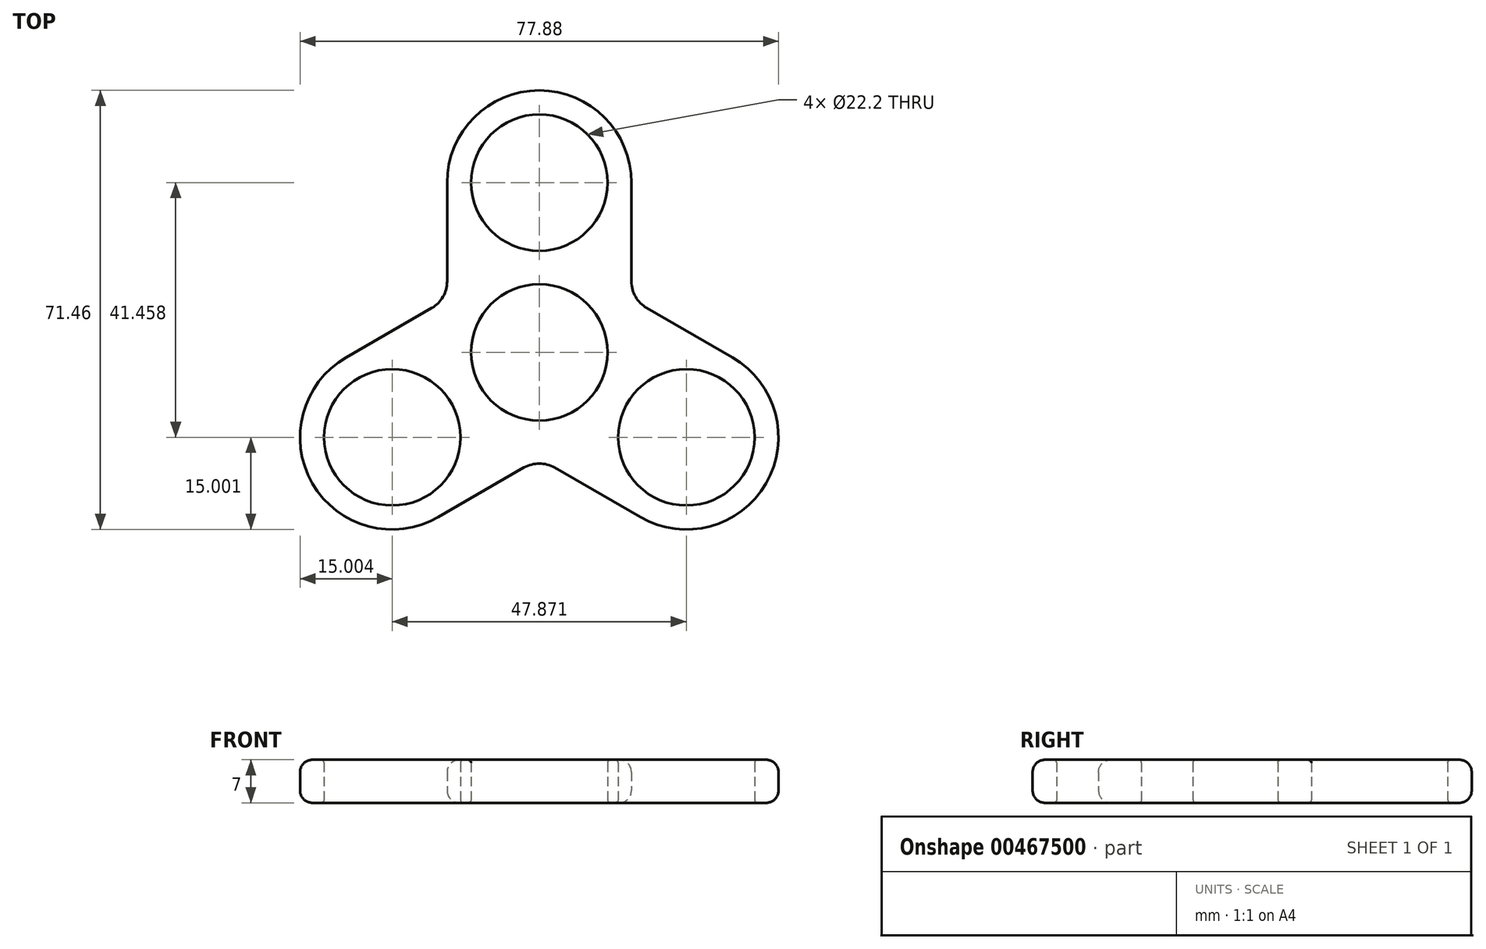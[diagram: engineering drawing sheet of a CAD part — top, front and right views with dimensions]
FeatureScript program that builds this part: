
annotation { "Feature Type Name" : "Feature", "Feature Type Description" : "" }
export const myFeature = defineFeature(function(context is Context, id is Id, definition is map)
    precondition{}
    {
        {
            var Q0;
            Q0=qCreatedBy(makeId("Top.planeOp"),FACE);
            var sketch = newSketch(context, id + "F0", { "sketchPlane" : qUnion([Q0])});
            skCircle(sketch, "E0", {"center": v(0, 27.64) * mm, "radius": 11.1 * mm});
            skLineSegment(sketch, "E1", {"start": v(0, 0) * mm, "end": v(0, 27.64) * mm, "construction": true});
            skCircle(sketch, "E2", {"center": v(0, 27.64) * mm, "radius": 15 * mm});
            skCircle(sketch, "E3", {"center": v(0, 0) * mm, "radius": 11.1 * mm});
            skLineSegment(sketch, "E4", {"start": v(-15, 27.64) * mm, "end": v(-15, 0) * mm});
            skLineSegment(sketch, "E5", {"start": v(15, 27.64) * mm, "end": v(15, 0) * mm});
            skLineSegment(sketch, "E6", {"start": v(-15, 0) * mm, "end": v(15, 0) * mm});
            skCircle(sketch, "E7.1.0", {"center": v(-23.94, -13.82) * mm, "radius": 11.1 * mm});
            skCircle(sketch, "E7.1.1", {"center": v(-23.94, -13.82) * mm, "radius": 15 * mm});
            skLineSegment(sketch, "E7.1.2", {"start": v(-31.44, -0.83) * mm, "end": v(-7.5, 13) * mm});
            skLineSegment(sketch, "E7.1.3", {"start": v(-16.44, -26.8) * mm, "end": v(7.5, -13) * mm});
            skCircle(sketch, "E7.2.0", {"center": v(23.94, -13.82) * mm, "radius": 11.1 * mm});
            skCircle(sketch, "E7.2.1", {"center": v(23.94, -13.82) * mm, "radius": 15 * mm});
            skLineSegment(sketch, "E7.2.2", {"start": v(16.44, -26.8) * mm, "end": v(-7.5, -13) * mm});
            skLineSegment(sketch, "E7.2.3", {"start": v(31.44, -0.83) * mm, "end": v(7.5, 13) * mm});
            skSolve(sketch);
        }
        {
            var Q0;
            Q0=makeQuery(id+"F0.imprint","IMPRINT",FACE,{"disambiguationData":[TD([[makeQuery(id+"F0.imprint","IMPRINT",EDGE,{"derivedFrom":sQuery(id+"F0.wireOp",EDGE,"E7.1.0")}),-1.0]])]});
            var Q1;
            {var subQ7=sQuery(id+"F0.wireOp",EDGE,"E6");var subQ10=sQuery(id+"F0.wireOp",EDGE,"E3");var subQ14=makeQuery(id+"F0.imprint","INTERSECT",VERTEX,{"disambiguationData":[OD(0.0)],"derivedFrom":[subQ10,subQ7]});Q1=makeQuery(id+"F0.imprint","IMPRINT",FACE,{"disambiguationData":[TD([[makeQuery(id+"F0.imprint","IMPRINT",EDGE,{"disambiguationData":[TD([[subQ14,-1.0]])],"derivedFrom":subQ10}),-1.0]])]});}
            var Q2;
            Q2=makeQuery(id+"F0.imprint","IMPRINT",FACE,{"disambiguationData":[TD([[makeQuery(id+"F0.imprint","IMPRINT",EDGE,{"derivedFrom":sQuery(id+"F0.wireOp",EDGE,"E7.2.0")}),-1.0]])]});
            var Q3;
            {var subQ1=sQuery(id+"F0.wireOp",EDGE,"E4");var subQ4=sQuery(id+"F0.wireOp",EDGE,"E2");var subQ5=makeQuery(id+"F0.imprint","INTERSECT",VERTEX,{"derivedFrom":[subQ4,subQ1]});Q3=makeQuery(id+"F0.imprint","IMPRINT",FACE,{"disambiguationData":[TD([[makeQuery(id+"F0.imprint","IMPRINT",EDGE,{"disambiguationData":[TD([[subQ5,-1.0]])],"derivedFrom":subQ4}),-1.0]])]});}
            var Q4;
            Q4=makeQuery(id+"F0.imprint","IMPRINT",FACE,{"disambiguationData":[TD([[makeQuery(id+"F0.imprint","IMPRINT",EDGE,{"derivedFrom":sQuery(id+"F0.wireOp",EDGE,"E0")}),-1.0]])]});
            extrude(context, id + "F1", {"entities" : qUnion([Q0, Q1, Q2, Q3, Q4]), "depth" : 7 * mm});
        }
        {
            var Q0;
            Q0=makeQuery(id+"F1.opExtrude","SWEPT_EDGE",EDGE,{"disambiguationData":[OSD([sQuery(id+"F0.wireOp",EDGE,"E4"),sQuery(id+"F0.wireOp",EDGE,"E7.1.2")])]});
            var Q1;
            Q1=makeQuery(id+"F1.opExtrude","SWEPT_EDGE",EDGE,{"disambiguationData":[OSD([sQuery(id+"F0.wireOp",EDGE,"E5"),sQuery(id+"F0.wireOp",EDGE,"E7.2.3")])]});
            var Q2;
            Q2=makeQuery(id+"F1.opExtrude","SWEPT_EDGE",EDGE,{"disambiguationData":[OSD([sQuery(id+"F0.wireOp",EDGE,"E7.1.3"),sQuery(id+"F0.wireOp",EDGE,"E7.2.2")])]});
            fillet(context, id + "F2", {"entities" : qUnion([Q0, Q1, Q2]), "radius" : 5 * mm, "tangentPropagation" : true, "allowEdgeOverflow" : false});
        }
        {
            var Q0;
            Q0=makeQuery(id+"F1.opExtrude","CAP_EDGE",EDGE,{"disambiguationData":[OSD([sQuery(id+"F0.wireOp",EDGE,"E0")])],"isStart":false});
            var Q1;
            Q1=makeQuery(id+"F1.opExtrude","CAP_EDGE",EDGE,{"disambiguationData":[OSD([sQuery(id+"F0.wireOp",EDGE,"E3")])],"isStart":false});
            var Q2;
            Q2=makeQuery(id+"F1.opExtrude","CAP_EDGE",EDGE,{"disambiguationData":[OSD([sQuery(id+"F0.wireOp",EDGE,"E7.1.0")])],"isStart":false});
            var Q3;
            Q3=makeQuery(id+"F1.opExtrude","CAP_EDGE",EDGE,{"disambiguationData":[OSD([sQuery(id+"F0.wireOp",EDGE,"E7.2.0")])],"isStart":false});
            var Q4;
            Q4=makeQuery(id+"F1.opExtrude","CAP_EDGE",EDGE,{"disambiguationData":[OSD([sQuery(id+"F0.wireOp",EDGE,"E7.1.0")])],"isStart":true});
            var Q5;
            Q5=makeQuery(id+"F1.opExtrude","CAP_EDGE",EDGE,{"disambiguationData":[OSD([sQuery(id+"F0.wireOp",EDGE,"E0")])],"isStart":true});
            var Q6;
            Q6=makeQuery(id+"F1.opExtrude","CAP_EDGE",EDGE,{"disambiguationData":[OSD([sQuery(id+"F0.wireOp",EDGE,"E7.2.0")])],"isStart":true});
            var Q7;
            Q7=makeQuery(id+"F1.opExtrude","CAP_EDGE",EDGE,{"disambiguationData":[OSD([sQuery(id+"F0.wireOp",EDGE,"E3")])],"isStart":true});
            fillet(context, id + "F3", {"entities" : qUnion([Q0, Q1, Q2, Q3, Q4, Q5, Q6, Q7]), "radius" : .5 * mm, "tangentPropagation" : true, "allowEdgeOverflow" : false});
        }
        {
            var Q0;
            Q0=makeQuery(id+"F1.opExtrude","SWEPT_FACE",FACE,{"disambiguationData":[OSD([sQuery(id+"F0.wireOp",EDGE,"E7.1.3")])]});
            var Q1;
            Q1=makeQuery(id+"F2.opFillet","BLEND_FACE",FACE,{"disambiguationData":[OSD([sQuery(id+"F0.wireOp",EDGE,"E7.1.3"),sQuery(id+"F0.wireOp",EDGE,"E7.2.2")])]});
            var Q2;
            Q2=makeQuery(id+"F1.opExtrude","SWEPT_FACE",FACE,{"disambiguationData":[OSD([sQuery(id+"F0.wireOp",EDGE,"E7.2.2")])]});
            var Q3;
            Q3=makeQuery(id+"F1.opExtrude","SWEPT_FACE",FACE,{"disambiguationData":[OSD([sQuery(id+"F0.wireOp",EDGE,"E7.2.1")])]});
            var Q4;
            Q4=makeQuery(id+"F1.opExtrude","SWEPT_FACE",FACE,{"disambiguationData":[OSD([sQuery(id+"F0.wireOp",EDGE,"E7.1.1")])]});
            var Q5;
            Q5=makeQuery(id+"F1.opExtrude","SWEPT_FACE",FACE,{"disambiguationData":[OSD([sQuery(id+"F0.wireOp",EDGE,"E7.1.2")])]});
            var Q6;
            Q6=makeQuery(id+"F2.opFillet","BLEND_FACE",FACE,{"disambiguationData":[OSD([sQuery(id+"F0.wireOp",EDGE,"E4"),sQuery(id+"F0.wireOp",EDGE,"E7.1.2")])]});
            var Q7;
            Q7=makeQuery(id+"F1.opExtrude","SWEPT_FACE",FACE,{"disambiguationData":[OSD([sQuery(id+"F0.wireOp",EDGE,"E4")])]});
            var Q8;
            Q8=makeQuery(id+"F1.opExtrude","SWEPT_FACE",FACE,{"disambiguationData":[OSD([sQuery(id+"F0.wireOp",EDGE,"E2")])]});
            var Q9;
            Q9=makeQuery(id+"F1.opExtrude","SWEPT_FACE",FACE,{"disambiguationData":[OSD([sQuery(id+"F0.wireOp",EDGE,"E5")])]});
            var Q10;
            Q10=makeQuery(id+"F2.opFillet","BLEND_FACE",FACE,{"disambiguationData":[OSD([sQuery(id+"F0.wireOp",EDGE,"E5"),sQuery(id+"F0.wireOp",EDGE,"E7.2.3")])]});
            var Q11;
            Q11=makeQuery(id+"F1.opExtrude","SWEPT_FACE",FACE,{"disambiguationData":[OSD([sQuery(id+"F0.wireOp",EDGE,"E7.2.3")])]});
            fillet(context, id + "F4", {"entities" : qUnion([Q0, Q1, Q2, Q3, Q4, Q5, Q6, Q7, Q8, Q9, Q10, Q11]), "radius" : 2 * mm, "tangentPropagation" : true, "allowEdgeOverflow" : false});
        }
    });
